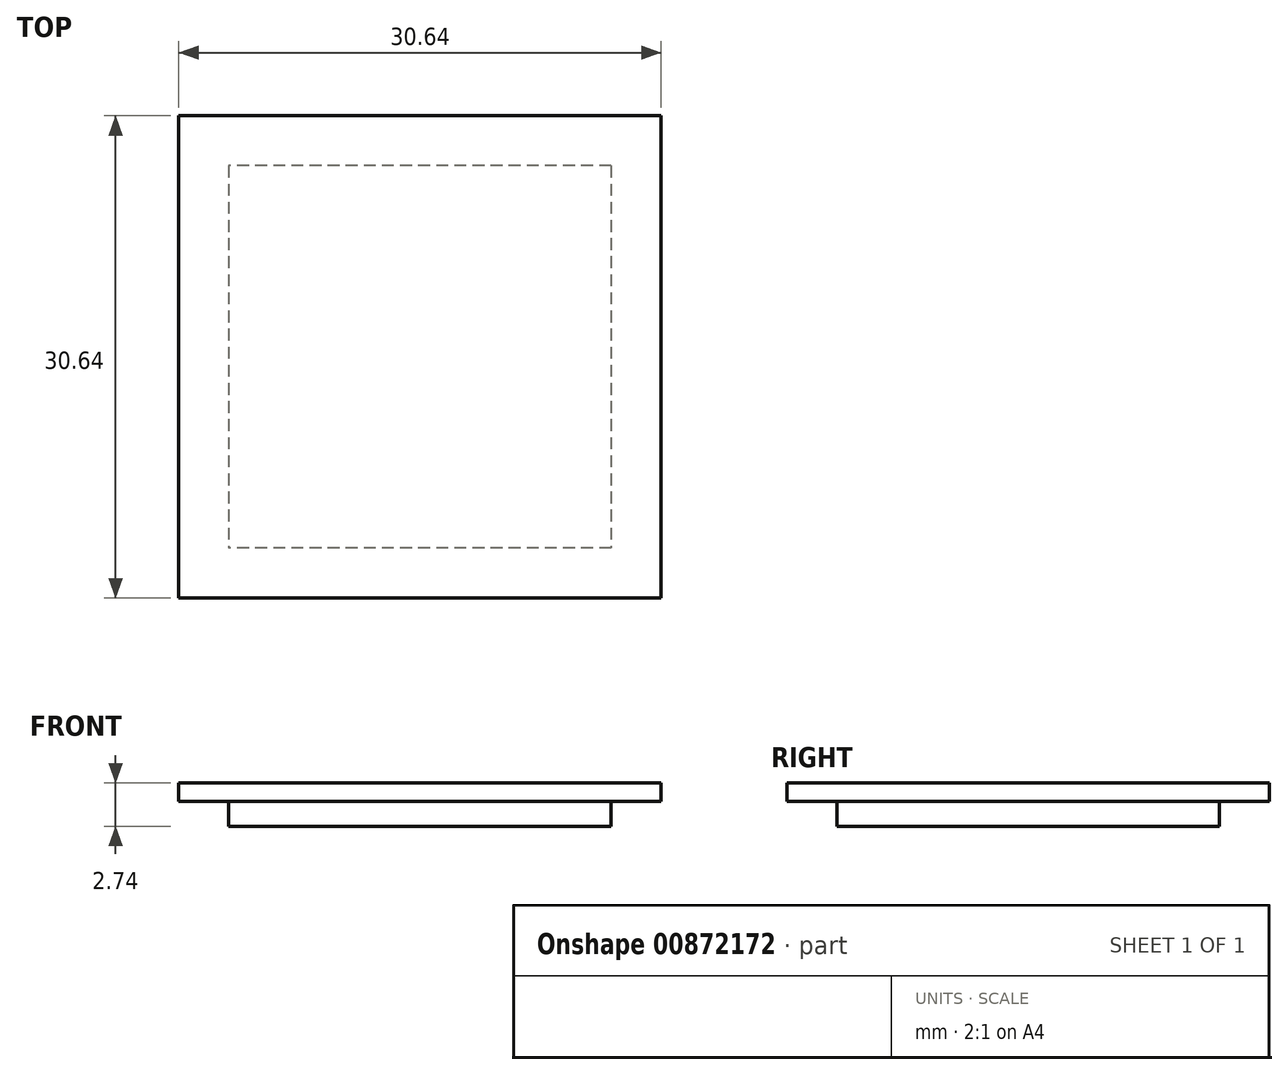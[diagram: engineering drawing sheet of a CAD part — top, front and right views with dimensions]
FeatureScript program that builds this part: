
annotation { "Feature Type Name" : "Feature", "Feature Type Description" : "" }
export const myFeature = defineFeature(function(context is Context, id is Id, definition is map)
    precondition{}
    {
        {
            var Q0;
            Q0=qCreatedBy(makeId("Top.planeOp"),FACE);
            var sketch = newSketch(context, id + "F0", { "sketchPlane" : qUnion([Q0])});
            skLineSegment(sketch, "E0.bottom", {"start": v(15.32, 15.32) * mm, "end": v(-15.32, 15.32) * mm});
            skLineSegment(sketch, "E0.top", {"start": v(15.32, -15.32) * mm, "end": v(-15.32, -15.32) * mm});
            skLineSegment(sketch, "E0.left", {"start": v(15.32, 15.32) * mm, "end": v(15.32, -15.32) * mm});
            skLineSegment(sketch, "E0.right", {"start": v(-15.32, 15.32) * mm, "end": v(-15.32, -15.32) * mm});
            skPoint(sketch, "E0.middle", {"position": v(0, 0) * mm});
            skLineSegment(sketch, "E1.0", {"start": v(12.14, 12.14) * mm, "end": v(-12.14, 12.14) * mm});
            skLineSegment(sketch, "E1.1", {"start": v(12.14, 12.14) * mm, "end": v(12.14, -12.14) * mm});
            skLineSegment(sketch, "E1.2", {"start": v(12.14, -12.14) * mm, "end": v(-12.14, -12.14) * mm});
            skLineSegment(sketch, "E1.3", {"start": v(-12.14, 12.14) * mm, "end": v(-12.14, -12.14) * mm});
            skSolve(sketch);
        }
        {
            var Q0;
            Q0=makeQuery(id+"F0.imprint","IMPRINT",FACE,{"disambiguationData":[TD([[makeQuery(id+"F0.imprint","IMPRINT",EDGE,{"derivedFrom":sQuery(id+"F0.wireOp",EDGE,"E0.bottom")}),1.0]])]});
            var Q1;
            Q1=makeQuery(id+"F0.imprint","IMPRINT",FACE,{"disambiguationData":[TD([[makeQuery(id+"F0.imprint","IMPRINT",EDGE,{"derivedFrom":sQuery(id+"F0.wireOp",EDGE,"E1.0")}),1.0]])]});
            extrude(context, id + "F1", {"entities" : qUnion([Q0, Q1]), "depth" : 1.17 * mm, "offsetDistance" : 25.4 * mm});
        }
        {
            var Q0;
            Q0=makeQuery(id+"F0.imprint","IMPRINT",FACE,{"disambiguationData":[TD([[makeQuery(id+"F0.imprint","IMPRINT",EDGE,{"derivedFrom":sQuery(id+"F0.wireOp",EDGE,"E1.0")}),1.0]])]});
            extrude(context, id + "F2", {"entities" : qUnion([Q0]), "operationType" : NewBodyOperationType.ADD, "surfaceOperationType" : NewSurfaceOperationType.ADD, "oppositeDirection" : true, "depth" : 1.57 * mm, "offsetDistance" : 25.4 * mm});
        }
    });
